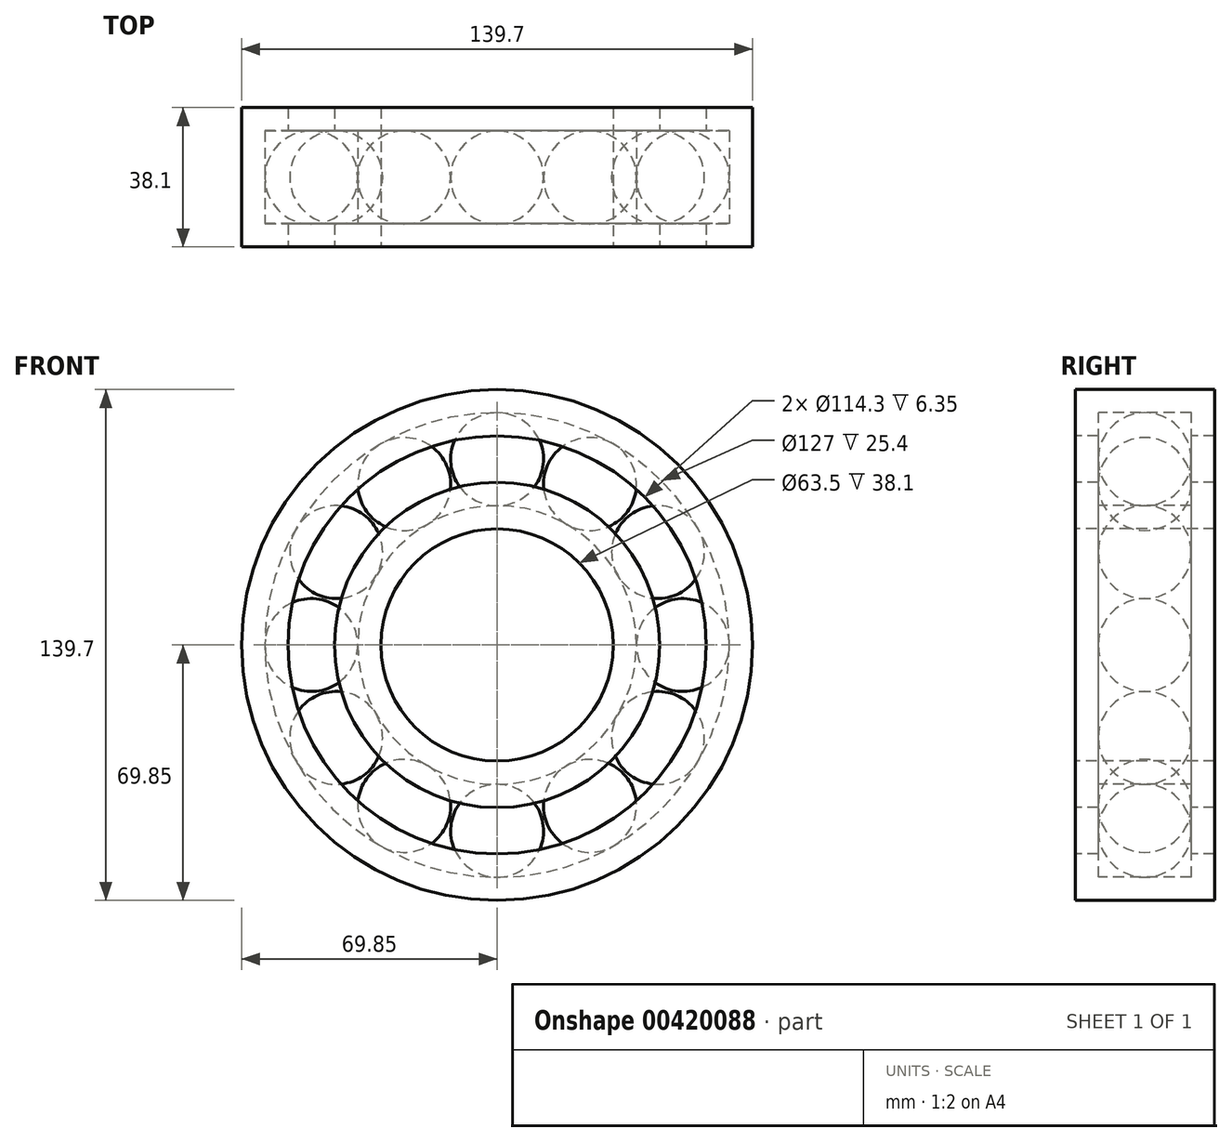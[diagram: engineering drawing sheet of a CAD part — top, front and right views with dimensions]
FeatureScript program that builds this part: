
annotation { "Feature Type Name" : "Feature", "Feature Type Description" : "" }
export const myFeature = defineFeature(function(context is Context, id is Id, definition is map)
    precondition{}
    {
        {
            var Q0;
            Q0=qCreatedBy(makeId("Top.planeOp"),FACE);
            var sketch = newSketch(context, id + "F0", { "sketchPlane" : qUnion([Q0])});
            skLineSegment(sketch, "E0.right", {"start": v(-63.5, 12.74) * mm, "end": v(-63.5, -12.66) * mm});
            skPoint(sketch, "E0.middle", {"position": v(-50.8, 0) * mm});
            skPoint(sketch, "E1.right.end.orphan", {"position": v(-57.15, -12.66) * mm});
            skLineSegment(sketch, "E2.trimOffspring", {"start": v(-57.15, -12.66) * mm, "end": v(-63.5, -12.66) * mm});
            skPoint(sketch, "E1.bottom.end.orphan", {"position": v(-57.15, 12.74) * mm});
            skLineSegment(sketch, "E3.trimOffspring", {"start": v(-57.15, 12.74) * mm, "end": v(-63.5, 12.74) * mm});
            skLineSegment(sketch, "E4.bottom", {"start": v(-57.15, 19.09) * mm, "end": v(-69.85, 19.09) * mm});
            skLineSegment(sketch, "E4.top", {"start": v(-57.15, -19.01) * mm, "end": v(-69.85, -19.01) * mm});
            skLineSegment(sketch, "E4.left", {"start": v(-57.15, 19.09) * mm, "end": v(-57.15, 12.74) * mm});
            skLineSegment(sketch, "E4.right", {"start": v(-69.85, 19.09) * mm, "end": v(-69.85, -19.01) * mm});
            skPoint(sketch, "E4.middle", {"position": v(-63.5, 0.04) * mm});
            skLineSegment(sketch, "E5.trimOffspring", {"start": v(-57.15, -12.66) * mm, "end": v(-57.15, -19.01) * mm});
            skLineSegment(sketch, "E6.MirrorCS", {"start": v(-44.45, 19.09) * mm, "end": v(-44.45, 12.74) * mm});
            skLineSegment(sketch, "E7.MirrorCS", {"start": v(-44.45, -12.66) * mm, "end": v(-44.45, -19.01) * mm});
            skLineSegment(sketch, "E8.MirrorCS", {"start": v(-44.45, -12.66) * mm, "end": v(-38.1, -12.66) * mm});
            skPoint(sketch, "E9.MirrorP", {"position": v(-38.1, 0.04) * mm});
            skLineSegment(sketch, "E10.MirrorCS", {"start": v(-38.1, 12.74) * mm, "end": v(-38.1, -12.66) * mm});
            skLineSegment(sketch, "E11.MirrorCS", {"start": v(-44.45, 12.74) * mm, "end": v(-38.1, 12.74) * mm});
            skPoint(sketch, "E12.MirrorP", {"position": v(-44.45, 12.74) * mm});
            skLineSegment(sketch, "E13.MirrorCS", {"start": v(-44.45, 19.09) * mm, "end": v(-31.75, 19.09) * mm});
            skPoint(sketch, "E14.MirrorP", {"position": v(-44.45, -12.66) * mm});
            skLineSegment(sketch, "E15.MirrorCS", {"start": v(-44.45, -19.01) * mm, "end": v(-31.75, -19.01) * mm});
            skLineSegment(sketch, "E16.MirrorCS", {"start": v(-31.75, 19.09) * mm, "end": v(-31.75, -19.01) * mm});
            skPoint(sketch, "E17.start.orphan", {"position": v(-63.5, -19.01) * mm});
            skSolve(sketch);
        }
        {
            var Q0;
            Q0=qCreatedBy(makeId("Top.planeOp"),FACE);
            var sketch = newSketch(context, id + "F1", { "sketchPlane" : qUnion([Q0])});
            skLineSegment(sketch, "E18", {"start": v(0, -31.05) * mm, "end": v(0, 33.02) * mm});
            skSolve(sketch);
        }
        {
            var Q0;
            Q0=qSketchRegion(id+"F0",true);
            var Q1;
            Q1=sQuery(id+"F1.wireOp",EDGE,"E18");
            revolve(context, id + "F2", {"entities" : qUnion([Q0]), "axis" : qUnion([Q1]), "revolveType" : RevolveType.FULL});
        }
        {
            var Q0;
            Q0=qCreatedBy(makeId("Top.planeOp"),FACE);
            var sketch = newSketch(context, id + "F3", { "sketchPlane" : qUnion([Q0])});
            skArc(sketch, "E19", {"start": v(-50.8, 12.7) * mm, "mid": v(-63.5, 0) * mm, "end": v(-50.8, -12.7) * mm});
            skLineSegment(sketch, "E20", {"start": v(-50.8, -12.7) * mm, "end": v(-50.8, 12.7) * mm});
            skSolve(sketch);
        }
        {
            var Q0;
            Q0=qCreatedBy(makeId("Top.planeOp"),FACE);
            var sketch = newSketch(context, id + "F4", { "sketchPlane" : qUnion([Q0])});
            skLineSegment(sketch, "E21", {"start": v(-50.8, 0) * mm, "end": v(-50.8, 33.54) * mm});
            skSolve(sketch);
        }
        {
            var Q0;
            Q0=qSketchRegion(id+"F3",true);
            var Q1;
            Q1=sQuery(id+"F4.wireOp",EDGE,"E21");
            revolve(context, id + "F5", {"entities" : qUnion([Q0]), "axis" : qUnion([Q1]), "revolveType" : RevolveType.FULL});
        }
        {
            var Q0;
            Q0=qCreatedBy(makeId("Top.planeOp"),FACE);
            var sketch = newSketch(context, id + "F6", { "sketchPlane" : qUnion([Q0])});
            skLineSegment(sketch, "E22", {"start": v(0, 0) * mm, "end": v(0, 54.11) * mm});
            skSolve(sketch);
        }
        {
            var Q0;
            Q0=makeQuery(id+"F5.opRevolve","SWEPT_BODY",BODY,{"disambiguationData":[OSD([sQuery(id+"F3.wireOp",EDGE,"E19"),sQuery(id+"F3.wireOp",EDGE,"E20")])]});
            var Q1;
            Q1=sQuery(id+"F6.wireOp",EDGE,"E22");
            circularPattern(context, id + "F7", {"entities" : qUnion([Q0]), "axis" : qUnion([Q1]), "angle" : 30 * degree, "instanceCount" : 13});
        }
    });
